# Revit family: WC MURANO
name_source: partatom
category: Plumbing Fixtures
revit_build: Autodesk Revit 2016 (Build: 20150714_1515(x64)
units: mm (PartAtom-declared; Revit-internal decimal feet)

## family parameters
Always vertical = Yes
Cut with Voids When Loaded = No
OmniClass Number = 23.45.00.00
OmniClass Title = Sanitary, Laundry, and Cleaning Equipment
Part Type = Normal
Room Calculation Point = No
Round Connector Dimension = Use Diameter
Shared = Yes
Work Plane-Based = Yes

## types (1)
- WC MURANO
    Accessories = Tapa de cierre lento con sistema de fijación. Reducción para válvula de admisión deØ15/16-14 NS-1 a 1/2-14 NPSM
    Características del Producto = Diseño ergonómico de construcción robusta con cerámica de 10mm de espesor, con sistema de descarga tipo vórtice con sifón jet y espejo de agua óptimo, mueblelibre de alabeo (base plana).
    Conexión de Alimentación = A la alimentacion Ø15/16-14 NS-1
    Conexión de Descarga = A la descarga se acopla al Ø de drenaje de 4" con brida sanitaria o cuello de cera.
    Default Elevation = 0.0"
    Description = WC con Trampa Oculta, una Descarga de 4.8 l, con Asiento de Cierre Lento
    Manufacturer = Helvex S.A. de C.V.
    Materials = Cerámica porcelanizada de alto brillo Grado de Calidad "A", Tipo I Trampa oculta
    Maximum Consumption = 4,8 lpd
    Modelo = WC MURANO
    Operation = Sistema de una descarga
    Presión Máxima de Trabajo = 6.0 psi
    Presión Mínima de Trabajo = 0.3 psi
    Type Comments = WC Murano
    URL = http://www.helvex.com
    Valves = Valv. de admisión y descarga certificadas, Valv. de admisión silenciosa, válvulas armadas y calibradas, válvula de descarga con sello hermético

## geometry (parser evidence)
native form markers: Sweep x3
no freeform markers — native parametric forms only
